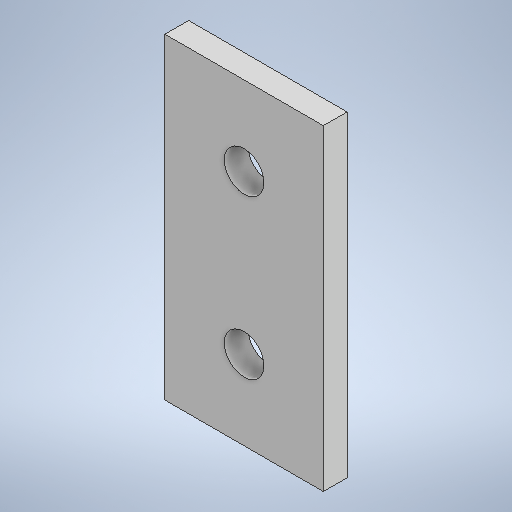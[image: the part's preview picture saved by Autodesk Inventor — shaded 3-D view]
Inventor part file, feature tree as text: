
AUTODESK INVENTOR PART (.ipt)
format: ipt  version: 2025.1 (Build 291241020, 241B)  size: 230,400 bytes
history: native  units: mm
features: extrude x1, sketch x1
ambient origin geometry x8: Origin, YZ Plane, XZ Plane, XY Plane, X Axis, Y Axis, Z Axis, Center Point
bodies: Solid1 (feature_tree)
feature tree (2):
  extrude  "Extrusion1"  Depth=20.0mm
  sketch  "Sketch1"  dims[d0=40.0mm d1=20.0mm d2=5.0mm d3=20.0mm d4=10.0mm d5=10.0mm d6=3.0mm d7=0.0mm]
